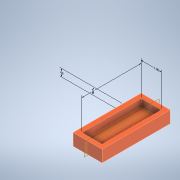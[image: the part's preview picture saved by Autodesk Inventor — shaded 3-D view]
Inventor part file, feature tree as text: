
AUTODESK INVENTOR PART (.ipt)
format: ipt  version: 2021 (Build 250183000, 183)  size: 131,584 bytes
history: native  units: in
note: dims shown in document units (in); Inventor stores cm internally (conversion verified against a paired STEP export)
features: other x4, extrude x2, sketch x2
ambient origin geometry x8: Origin, YZ Plane, XZ Plane, XY Plane, X Axis, Y Axis, Z Axis, Center Point
bodies: Solid1 (feature_tree)
feature tree (8):
  other  "Annotations"
  extrude  "Extrusion1"  Depth=0.375in
  extrude  "Extrusion2"  Depth=0.625in TaperAngle=0.0deg
  sketch  "Sketch1"  dims[d2=0.375in d3=0.0in d1=0.375in]
  sketch  "Sketch2"  dims[d5=0.375in d4=0.625in d7=0.0in d10=1.7in d11=0.0in d12=0.3937in d13=5.0in d20=0.0925in d21=0.1005in d22=0.625in d8=0.0in d9=0.3937in]
  other  "Linear Dimension 1"
  other  "Linear Dimension 2"
  other  "Linear Dimension 3"
